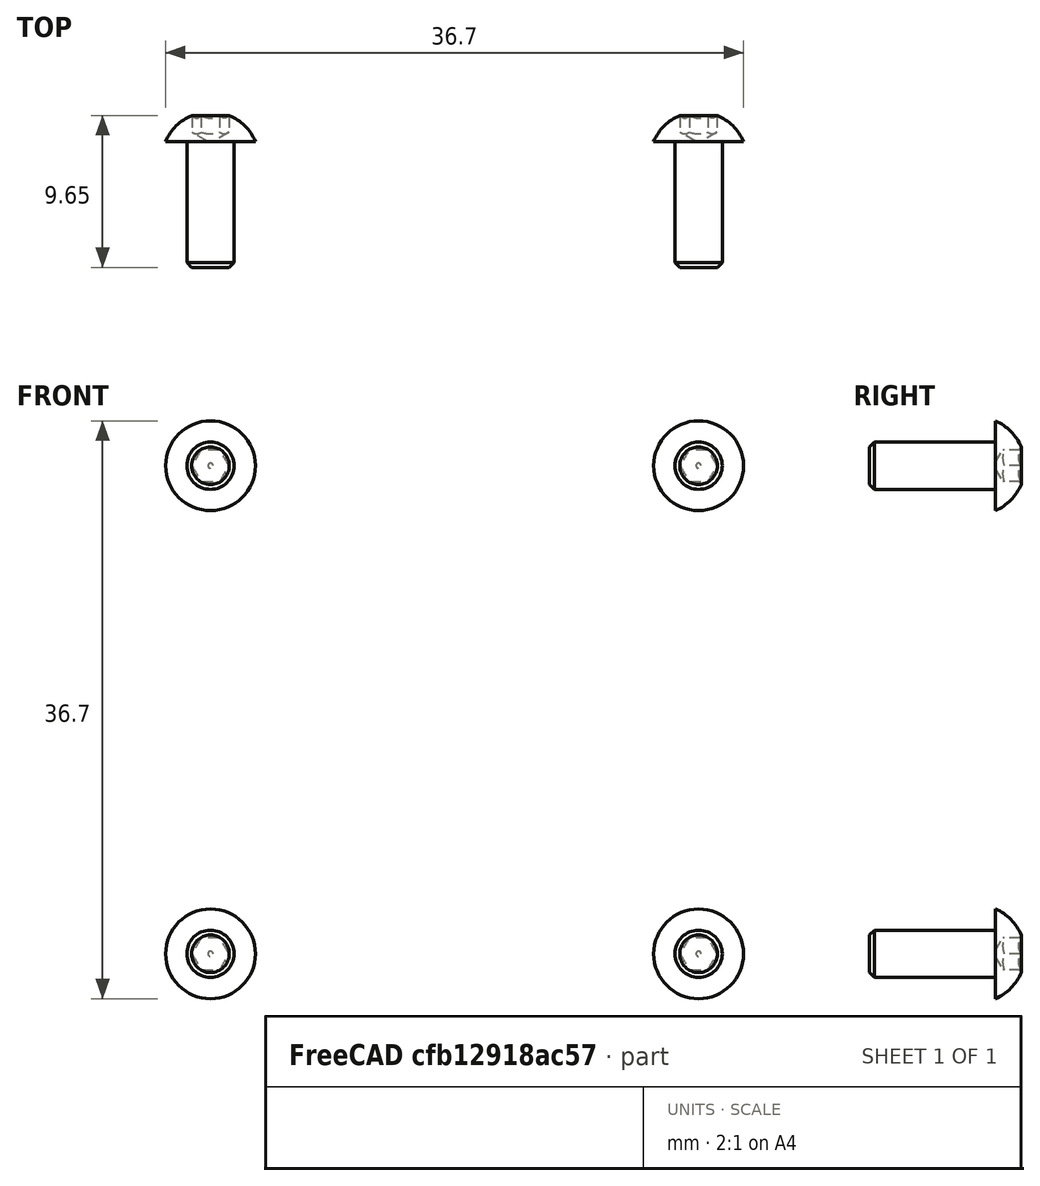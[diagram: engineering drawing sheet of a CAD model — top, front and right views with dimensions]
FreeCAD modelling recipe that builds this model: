
FCSTD DOCUMENT  (FreeCAD 0.20R29410 (Git))
Label: ASM_DriveUnit
License: All rights reserved
LicenseURL: http://en.wikipedia.org/wiki/All_rights_reserved
objects: App::DocumentObjectGroup×4, Part::FeaturePython×4, App::Link×2, PartDesign::CoordinateSystem×1, App::FeaturePython×1, App::Part×1
note: 5 computed .brp shape members not serialized (recipe doc carries the construction recipe); baked Part::Feature solids carry a one-line shape summary decoded from their .brp
EXTERNAL_REF file=ASM_Stepper.FCStd obj=LCS_Origin
EXTERNAL_REF file=ASM_Stepper.FCStd obj=Assembly
EXTERNAL_REF file=ASM_DriveWheel.FCStd obj=LCS_Origin
EXTERNAL_REF file=ASM_Stepper.FCStd obj=Stepper_LCS_mount
EXTERNAL_REF file=ASM_DriveWheel.FCStd obj=Assembly
EXTERNAL_REF file=MotorBracket.FCStd obj=Body001
EXTERNAL_REF file=MotorBracket.FCStd obj=Mirrored001

FEATURE [App::DocumentObjectGroup] Parts
FEATURE [PartDesign::CoordinateSystem] LCS_Origin
  AttacherType = Attacher::AttachEngine3D
  MapMode = 2
  Support = -> [X_Axis]
FEATURE [App::FeaturePython] Variables  # WARN: FeaturePython — macro-defined, semantics opaque (R4)
  Type = App::PropertyContainer
FEATURE [App::DocumentObjectGroup] Constraints
FEATURE [App::DocumentObjectGroup] Configurations
FEATURE [App::Link] ASM_Stepper
  AttachedBy = #LCS_Origin
  AttachedTo = Parent Assembly#LCS_Origin
  LinkedObject = -> <external ASM_Stepper.FCStd>#Assembly
  SolverId = Asm4EE
  expr: Placement = LCS_Origin.Placement * AttachmentOffset * ASM_Stepper#LCS_Origin.Placement ^ -1
FEATURE [App::Link] ASM_DriveWheel
  AttachedBy = #LCS_Origin
  AttachedTo = ASM_Stepper#Stepper_LCS_mount
  AttachmentOffset = pos=(0,0,-14) rot=(0,0,1;0rad)
  LinkPlacement = pos=(0,11,30) rot=(1,0,0;1.5708rad)
  LinkedObject = -> <external ASM_DriveWheel.FCStd>#Assembly
  Placement = pos=(0,11,30) rot=(1,0,0;1.5708rad)
  SolverId = Asm4EE
  expr: Placement = ASM_Stepper.Placement * ASM_Stepper#Stepper_LCS_mount.Placement * AttachmentOffset * ASM_DriveWheel#LCS_Origin.Placement ^ -1
FEATURE [Part::FeaturePython] Screw  label="M3x8-Screw"  # Fasteners workbench fastener (typed FeaturePython)
  Placement = pos=(-15.5,-8.88e-14,45.5) rot=(-1,0,0;1.5708rad)
  baseObject = -> <external MotorBracket.FCStd>#Body001 [Edge90]
  diameter = 1
  invert = true
  length = 1
  lengthCustom = 8
  matchOuter = true
  offset = 0
  thread = false
  type = 40
FEATURE [Part::FeaturePython] Screw001  label="M3x8-Screw007"  # Fasteners workbench fastener (typed FeaturePython)
  Placement = pos=(15.5,-7e-15,45.5) rot=(-1,0,0;1.5708rad)
  baseObject = -> <external MotorBracket.FCStd>#Mirrored001 [Edge87]
  diameter = 1
  invert = true
  length = 1
  lengthCustom = 8
  matchOuter = true
  offset = 0
  thread = false
  type = 40
FEATURE [Part::FeaturePython] Screw002  label="M3x8-Screw008"  # Fasteners workbench fastener (typed FeaturePython)
  Placement = pos=(15.5,-7e-15,14.5) rot=(-1,0,0;1.5708rad)
  baseObject = -> <external MotorBracket.FCStd>#Mirrored001 [Edge88]
  diameter = 1
  invert = true
  length = 1
  lengthCustom = 8
  matchOuter = true
  offset = 0
  thread = false
  type = 40
FEATURE [Part::FeaturePython] Screw003  label="M3x8-Screw009"  # Fasteners workbench fastener (typed FeaturePython)
  Placement = pos=(-15.5,-7e-15,14.5) rot=(-1,0,0;1.5708rad)
  baseObject = -> <external MotorBracket.FCStd>#Mirrored001 [Edge91]
  diameter = 1
  invert = true
  length = 1
  lengthCustom = 8
  matchOuter = true
  offset = 0
  thread = false
  type = 40
FEATURE [App::DocumentObjectGroup] Fasteners
  Group = -> [Screw,Screw001,Screw002,Screw003]
FEATURE [App::Part] Assembly
  AssemblyType = Part::Link
  Group = -> [LCS_Origin,Variables,Constraints,Configurations,ASM_Stepper,ASM_DriveWheel,Fasteners,Screw,Screw001,Screw002,Screw003]
  Origin = -> Origin
  Type = Assembly

RESOLVED EXTERNAL PARTS (link-assembly join: the EXTERNAL_REF files above that resolve inside this repo's crawl, each included once):
---- part ASM_DriveWheel.FCStd = doc fcstd_1d94934c7a89 ----
FCSTD DOCUMENT  (FreeCAD 0.20R29410 (Git))
Label: ASM_DriveWheel
License: All rights reserved
LicenseURL: http://en.wikipedia.org/wiki/All_rights_reserved
objects: App::DocumentObjectGroup×3, App::Link×3, PartDesign::CoordinateSystem×1, App::FeaturePython×1, App::Part×1
note: 1 computed .brp shape members not serialized (recipe doc carries the construction recipe); baked Part::Feature solids carry a one-line shape summary decoded from their .brp
EXTERNAL_REF file=DriveWheelHub.FCStd obj=LCS_Mount
EXTERNAL_REF file=FlangeHub5mm.FCStd obj=LCS_Origin
EXTERNAL_REF file=DriveWheelHub.FCStd obj=Assembly
EXTERNAL_REF file=FlangeHub5mm.FCStd obj=Assembly
EXTERNAL_REF file=DriveWheelHub.FCStd obj=LCS_Origin
EXTERNAL_REF file=DriveWheelTire.FCStd obj=LCS_Origin
EXTERNAL_REF file=DriveWheelTire.FCStd obj=Assembly

FEATURE [App::DocumentObjectGroup] Parts
FEATURE [PartDesign::CoordinateSystem] LCS_Origin
  AttacherType = Attacher::AttachEngine3D
  MapMode = 2
  Support = -> [X_Axis]
FEATURE [App::FeaturePython] Variables  # WARN: FeaturePython — macro-defined, semantics opaque (R4)
  Type = App::PropertyContainer
FEATURE [App::DocumentObjectGroup] Constraints
FEATURE [App::DocumentObjectGroup] Configurations
FEATURE [App::Link] DriveWheelHub
  AttachedBy = #LCS_Mount
  AttachedTo = FlangeHub5mm#LCS_Origin
  AttachmentOffset = pos=(0,0,0) rot=(1,0,0;3.14159rad)
  LinkPlacement = pos=(0,5e-16,2) rot=(0,0,1;0rad)
  LinkedObject = -> <external DriveWheelHub.FCStd>#Assembly
  Placement = pos=(0,5e-16,2) rot=(0,0,1;0rad)
  SolverId = Asm4EE
  expr: Placement = FlangeHub5mm.Placement * FlangeHub5mm#LCS_Origin.Placement * AttachmentOffset * DriveWheelHub#LCS_Mount.Placement ^ -1
FEATURE [App::Link] FlangeHub5mm
  AttachedBy = #LCS_Origin
  AttachedTo = Parent Assembly#LCS_Origin
  AttachmentOffset = pos=(0,0,0) rot=(1,0,0;3.14159rad)
  LinkPlacement = pos=(0,0,0) rot=(1,0,0;3.14159rad)
  LinkedObject = -> <external FlangeHub5mm.FCStd>#Assembly
  Placement = pos=(0,0,0) rot=(1,0,0;3.14159rad)
  SolverId = Asm4EE
  expr: Placement = LCS_Origin.Placement * AttachmentOffset * FlangeHub5mm#LCS_Origin.Placement ^ -1
FEATURE [App::Link] DriveWheelTire
  AttachedBy = #LCS_Origin
  AttachedTo = DriveWheelHub#LCS_Origin
  LinkPlacement = pos=(0,5e-16,2) rot=(0,0,1;0rad)
  LinkedObject = -> <external DriveWheelTire.FCStd>#Assembly
  Placement = pos=(0,5e-16,2) rot=(0,0,1;0rad)
  SolverId = Asm4EE
  expr: Placement = DriveWheelHub.Placement * DriveWheelHub#LCS_Origin.Placement * AttachmentOffset * DriveWheelTire#LCS_Origin.Placement ^ -1
FEATURE [App::Part] Assembly
  AssemblyType = Part::Link
  Group = -> [LCS_Origin,Variables,Constraints,Configurations,DriveWheelHub,FlangeHub5mm,DriveWheelTire]
  Origin = -> Origin
  Type = Assembly
---- part ASM_Stepper.FCStd = doc fcstd_c9ab55faeef8 ----
FCSTD DOCUMENT  (FreeCAD 0.20R29410 (Git))
Label: ASM_Stepper
License: All rights reserved
LicenseURL: http://en.wikipedia.org/wiki/All_rights_reserved
objects: App::DocumentObjectGroup×3, PartDesign::CoordinateSystem×2, App::Link×2, App::FeaturePython×1, App::Part×1
note: 2 computed .brp shape members not serialized (recipe doc carries the construction recipe); baked Part::Feature solids carry a one-line shape summary decoded from their .brp
EXTERNAL_REF file=MotorBracket.FCStd obj=LCS_motor_mount
EXTERNAL_REF file=Stepper17.FCStd obj=LCS_mount
EXTERNAL_REF file=Stepper17.FCStd obj=Body
EXTERNAL_REF file=MotorBracket.FCStd obj=LCS_bottom
EXTERNAL_REF file=MotorBracket.FCStd obj=Assembly

FEATURE [App::DocumentObjectGroup] Parts
FEATURE [PartDesign::CoordinateSystem] LCS_Origin
  AttacherType = Attacher::AttachEngine3D
  MapMode = 2
  Support = -> [X_Axis]
FEATURE [App::FeaturePython] Variables  # WARN: FeaturePython — macro-defined, semantics opaque (R4)
  Type = App::PropertyContainer
FEATURE [App::DocumentObjectGroup] Constraints
FEATURE [App::DocumentObjectGroup] Configurations
FEATURE [App::Link] Stepper
  AssemblyType = Part::Link
  AttachedBy = #LCS_mount
  AttachedTo = MotorBracket#LCS_motor_mount
  LinkPlacement = pos=(0,-3,30) rot=(1,0,0;1.5708rad)
  LinkedObject = -> <external Stepper17.FCStd>#Body
  Placement = pos=(0,-3,30) rot=(1,0,0;1.5708rad)
  SolverId = Asm4EE
  expr: Placement = MotorBracket.Placement * MotorBracket#LCS_motor_mount.Placement * AttachmentOffset * Stepper17#LCS_mount.Placement ^ -1
FEATURE [App::Link] MotorBracket
  AttachedBy = #LCS_bottom
  AttachedTo = Parent Assembly#LCS_Origin
  LinkedObject = -> <external MotorBracket.FCStd>#Assembly
  SolverId = Asm4EE
  expr: Placement = LCS_Origin.Placement * AttachmentOffset * MotorBracket#LCS_bottom.Placement ^ -1
FEATURE [PartDesign::CoordinateSystem] Stepper_LCS_mount
  AttachedBy = Origin
  AttacherType = Attacher::AttachEngine3D
  Placement = pos=(0,-3,30) rot=(1,0,0;1.5708rad)
  SolverId = Asm4EE
  expr: Placement = Stepper.Placement * Stepper17#LCS_mount.Placement
FEATURE [App::Part] Assembly
  AssemblyType = Part::Link
  Group = -> [LCS_Origin,Variables,Constraints,Configurations,Stepper,MotorBracket,Stepper_LCS_mount]
  Origin = -> Origin
  Type = Assembly
---- part MotorBracket.FCStd = doc fcstd_789c5c22f6de ----
FCSTD DOCUMENT  (FreeCAD 0.20R29410 (Git))
Label: MotorBracket
License: All rights reserved
LicenseURL: http://en.wikipedia.org/wiki/All_rights_reserved
objects: Sketcher::SketchObject×5, PartDesign::Pocket×3, App::DocumentObjectGroup×3, PartDesign::Pad×2, PartDesign::Mirrored×2, PartDesign::CoordinateSystem×2, PartDesign::Plane×1, PartDesign::Body×1, App::FeaturePython×1, App::Part×1
note: 21 computed .brp shape members not serialized (recipe doc carries the construction recipe); baked Part::Feature solids carry a one-line shape summary decoded from their .brp

FEATURE [Sketcher::SketchObject] Sketch001
  FullyConstrained = true
  MapMode = 5
  Placement = pos=(0,0,0) rot=(0.57735,0.57735,0.57735;2.0944rad)
  Support = -> [YZ_Plane001]
  expr: Constraints[10] = <<Variables>>.SheetMetalThickness
  sketch-geometry (10):
    g0: LineSegment StartX=-3 StartY=4 StartZ=0 EndX=-3 EndY=51 EndZ=0
    g1: LineSegment StartX=-3 StartY=51 StartZ=0 EndX=0 EndY=51 EndZ=0
    g2: LineSegment StartX=0 StartY=51 StartZ=0 EndX=0 EndY=4 EndZ=0
    g3: LineSegment StartX=-4 StartY=0 StartZ=0 EndX=-51 EndY=0 EndZ=0
    g4: LineSegment StartX=-51 StartY=0 StartZ=0 EndX=-51 EndY=3 EndZ=0
    g5: LineSegment StartX=-51 StartY=3 StartZ=0 EndX=-4 EndY=3 EndZ=0
    g6: ArcOfCircle CenterX=-4 CenterY=4 CenterZ=0 NormalX=0 NormalY=0 NormalZ=1 AngleXU=0 Radius=1 StartAngle=4.71239 EndAngle=6.28319
    g7: GeomPoint X=-3 Y=3 Z=0
    g8: ArcOfCircle CenterX=-4 CenterY=4 CenterZ=0 NormalX=0 NormalY=0 NormalZ=1 AngleXU=0 Radius=4 StartAngle=4.71239 EndAngle=6.28319
    g9: GeomPoint X=0 Y=0 Z=0
  constraints (24):
    c: Coincident(g0,g1)
    c: Coincident(g1,g2)
    c: Horizontal(g1)
    c: Vertical(g0)
    c: Vertical(g2)
    c: Coincident(g3,g4)
    c: Coincident(g4,g5)
    c: Horizontal(g3)
    c: Horizontal(g5)
    c: Vertical(g4)
    c: DistanceX(g1,g1) = 3
    c: DistanceY(g9,g2) = 51
    c: Distance(g9,g3) = 51
    c: Coincident(g9,g-1)
    c: PointOnObject(g7,g0)
    c: PointOnObject(g7,g5)
    c: Tangent(g0,g6) = -1.5708
    c: Tangent(g5,g6) = -1.5708
    c: PointOnObject(g9,g2)
    c: PointOnObject(g9,g3)
    c: Tangent(g2,g8) = 1.5708
    c: Tangent(g3,g8) = 1.5708
    c: Radius(g6) = 1
    c: Coincident(g8,g6)
FEATURE [PartDesign::Pad] Pad001
  Direction = (1,-2e-16,3e-16)
  Length = 51
  Length2 = 25
  Midplane = true
  Placement = pos=(0,0,0) rot=(0.57735,0.57735,0.57735;2.0944rad)
  Profile = -> Sketch001
  ReferenceAxis = -> Sketch001 [N_Axis]
  Type = 0
FEATURE [Sketcher::SketchObject] Sketch002
  AttachmentOffset = pos=(0,30,0) rot=(0,0,1;0rad)
  FullyConstrained = true
  MapMode = 5
  Placement = pos=(0,-6.7e-15,30) rot=(1,0,0;1.5708rad)
  Support = -> [XZ_Plane001]
  sketch-geometry (10):
    g0: Circle CenterX=15.5 CenterY=15.5 CenterZ=0 NormalX=0 NormalY=0 NormalZ=1 AngleXU=0 Radius=1.6
    g1: LineSegment StartX=-15.5 StartY=15.5 StartZ=0 EndX=-15.5 EndY=-15.5 EndZ=0
    g2: LineSegment StartX=-15.5 StartY=-15.5 StartZ=0 EndX=15.5 EndY=-15.5 EndZ=0
    g3: LineSegment StartX=15.5 StartY=-15.5 StartZ=0 EndX=15.5 EndY=15.5 EndZ=0
    g4: LineSegment StartX=15.5 StartY=15.5 StartZ=0 EndX=-15.5 EndY=15.5 EndZ=0
    g5: GeomPoint X=0 Y=0 Z=0
    g6: Circle CenterX=0 CenterY=0 CenterZ=0 NormalX=0 NormalY=0 NormalZ=1 AngleXU=0 Radius=11
    g7: Circle CenterX=-15.5 CenterY=15.5 CenterZ=0 NormalX=0 NormalY=0 NormalZ=1 AngleXU=0 Radius=1.6
    g8: Circle CenterX=-15.5 CenterY=-15.5 CenterZ=0 NormalX=0 NormalY=0 NormalZ=1 AngleXU=0 Radius=1.6
    g9: Circle CenterX=15.5 CenterY=-15.5 CenterZ=0 NormalX=0 NormalY=0 NormalZ=1 AngleXU=0 Radius=1.6
  constraints (22):
    c: Diameter(g0) = 3.2
    c: Coincident(g1,g2)
    c: Coincident(g2,g3)
    c: Coincident(g3,g4)
    c: Coincident(g4,g1)
    c: Horizontal(g2)
    c: Horizontal(g4)
    c: Vertical(g1)
    c: Vertical(g3)
    c: Symmetric(g2,g1,g5)
    c: Equal(g3,g4)
    c: DistanceX(g4,g4) = 31
    c: Coincident(g0,g3)
    c: Coincident(g6,g5)
    c: Diameter(g6) = 22
    c: Coincident(g7,g1)
    c: Coincident(g8,g1)
    c: Coincident(g9,g2)
    c: Equal(g9,g8)
    c: Equal(g8,g7)
    c: Equal(g7,g0)
    c: Coincident(g6,g-1)
FEATURE [PartDesign::Pocket] Pocket001  label="MountHoles"
  BaseFeature = -> Pad001
  Direction = (0,1,2e-16)
  Length = 5
  Length2 = 100
  Placement = pos=(0,0,0) rot=(0.57735,0.57735,0.57735;2.0944rad)
  Profile = -> Sketch002
  Reversed = true
  Type = 1
FEATURE [Sketcher::SketchObject] Sketch003
  FullyConstrained = true
  MapMode = 5
  Support = -> [XY_Plane001]
  sketch-geometry (6):
    g0: LineSegment StartX=-12.865 StartY=0 StartZ=0 EndX=-12.865 EndY=-10.15 EndZ=0
    g1: ArcOfCircle CenterX=-12.865 CenterY=-10.15 CenterZ=0 NormalX=0 NormalY=0 NormalZ=1 AngleXU=0 Radius=2.15 StartAngle=4e-16 EndAngle=3.1416
    g2: ArcOfCircle CenterX=-12.865 CenterY=-39.85 CenterZ=0 NormalX=0 NormalY=0 NormalZ=1 AngleXU=0 Radius=2.15 StartAngle=3.14159 EndAngle=6.28319
    g3: LineSegment StartX=-10.715 StartY=-10.15 StartZ=0 EndX=-10.715 EndY=-39.85 EndZ=0
    g4: LineSegment StartX=-15.015 StartY=-10.15 StartZ=0 EndX=-15.015 EndY=-39.85 EndZ=0
    g5: LineSegment StartX=-12.865 StartY=-39.85 StartZ=0 EndX=0 EndY=-39.85 EndZ=0
  constraints (17):
    c: PointOnObject(g0,g-1)
    c: Vertical(g0)
    c: DistanceY(g0,g0) = 10.15
    c: Coincident(g1,g0)
    c: Equal(g2,g1)
    c: Vertical(g3)
    c: Vertical(g4)
    c: Coincident(g5,g2)
    c: PointOnObject(g5,g-2)
    c: Horizontal(g5)
    c: Tangent(g1,g3) = 1.5708
    c: Coincident(g1,g4)
    c: Tangent(g2,g4) = -1.5708
    c: Tangent(g2,g3) = 1.5708
    c: DistanceX(g5,g5) = 12.865
    c: Distance(g1,g1) = 4.3
    c: Distance(g1,g2) = 29.7
FEATURE [PartDesign::Pocket] Pocket002  label="BottomSlot"
  BaseFeature = -> Pocket001
  Direction = (0,0,-1)
  Length = 5
  Length2 = 100
  Placement = pos=(0,0,0) rot=(0.57735,0.57735,0.57735;2.0944rad)
  Profile = -> Sketch003
  Reversed = true
  Type = 1
FEATURE [Sketcher::SketchObject] Sketch
  AttachmentOffset = pos=(0,0,-25.5) rot=(0,0,1;0rad)
  FullyConstrained = true
  MapMode = 5
  Placement = pos=(-25.5,5.7e-15,-5.7e-15) rot=(0.57735,0.57735,0.57735;2.0944rad)
  Support = -> [YZ_Plane001]
  expr: .AttachmentOffset.Base.z = <<Pad001>>.Length / -2
  sketch-geometry (8):
    g0: LineSegment StartX=-3 StartY=23 StartZ=0 EndX=-23 EndY=3 EndZ=0
    g1: LineSegment StartX=-3 StartY=3 StartZ=0 EndX=-3 EndY=0 EndZ=0
    g2: LineSegment StartX=-3 StartY=0 StartZ=0 EndX=0 EndY=0 EndZ=0
    g3: LineSegment StartX=-3 StartY=3 StartZ=0 EndX=-3 EndY=5 EndZ=0
    g4: LineSegment StartX=-3 StartY=5 StartZ=0 EndX=-3 EndY=23 EndZ=0
    g5: LineSegment StartX=-23 StartY=3 StartZ=0 EndX=-5 EndY=3 EndZ=0
    g6: LineSegment StartX=-5 StartY=3 StartZ=0 EndX=-3 EndY=3 EndZ=0
    g7: LineSegment StartX=-5 StartY=3 StartZ=0 EndX=-3 EndY=5 EndZ=0
  constraints (22):
    c: Coincident(g0,g5)
    c: Coincident(g4,g0)
    c: DistanceY(g3,g4) = 20
    c: Coincident(g3,g6)
    c: DistanceY(g-1,g6) = 3
    c: Coincident(g1,g6)
    c: PointOnObject(g1,g-1)
    c: Coincident(g2,g1)
    c: Coincident(g2,g-1)
    c: Vertical(g1)
    c: Equal(g1,g2)
    c: Coincident(g3,g4)
    c: Vertical(g3)
    c: Vertical(g4)
    c: Coincident(g5,g6)
    c: Horizontal(g5)
    c: Horizontal(g6)
    c: Coincident(g7,g5)
    c: Coincident(g7,g4)
    c: Equal(g3,g6)
    c: DistanceX(g6,g6) = 2
    c: Equal(g4,g5)
FEATURE [PartDesign::Pad] Pad  label="Rib"
  BaseFeature = -> Pocket002
  Direction = (1,-2e-16,3e-16)
  Length = 3
  Length2 = 10
  Placement = pos=(0,0,0) rot=(0.57735,0.57735,0.57735;2.0944rad)
  Profile = -> Sketch
  ReferenceAxis = -> Sketch [N_Axis]
  Type = 0
  expr: Length = <<Variables>>.SheetMetalThickness
FEATURE [PartDesign::Mirrored] Mirrored
  BaseFeature = -> Pad
  MirrorPlane = -> YZ_Plane001
  Originals = -> [Pocket002,Pad]
  Placement = pos=(0,0,0) rot=(0.57735,0.57735,0.57735;2.0944rad)
FEATURE [Sketcher::SketchObject] Sketch004
  FullyConstrained = true
  MapMode = 5
  Placement = pos=(0,0,0) rot=(1,0,0;1.5708rad)
  Support = -> [XZ_Plane001]
  sketch-geometry (6):
    g0: LineSegment StartX=-72.5 StartY=0 StartZ=0 EndX=0 EndY=72.5 EndZ=0
    g1: LineSegment StartX=0 StartY=72.5 StartZ=0 EndX=72.5 EndY=0 EndZ=0
    g2: LineSegment StartX=72.5 StartY=0 StartZ=0 EndX=72.5 EndY=145 EndZ=0
    g3: LineSegment StartX=-72.5 StartY=0 StartZ=0 EndX=-72.5 EndY=145 EndZ=0
    g4: LineSegment StartX=-72.5 StartY=145 StartZ=0 EndX=72.5 EndY=145 EndZ=0
    g5: LineSegment StartX=-21.5 StartY=51 StartZ=0 EndX=21.5 EndY=51 EndZ=0
  constraints (19):
    c: PointOnObject(g0,g-1)
    c: PointOnObject(g0,g-2)
    c: Coincident(g1,g0)
    c: PointOnObject(g1,g-1)
    c: Coincident(g2,g1)
    c: Vertical(g2)
    c: Coincident(g3,g0)
    c: Vertical(g3)
    c: Coincident(g4,g3)
    c: Coincident(g4,g2)
    c: Horizontal(g4)
    c: Equal(g1,g0)
    c: Angle(g1,g-1) = 0.785398
    c: Equal(g2,g4)
    c: PointOnObject(g5,g0)
    c: PointOnObject(g5,g1)
    c: Horizontal(g5)
    c: DistanceY(g-1,g5) = 51
    c: DistanceX(g5,g5) = 43
FEATURE [PartDesign::Pocket] Pocket  label="CornerChamfer"
  BaseFeature = -> Mirrored
  Direction = (0,1,2e-16)
  Length = 5
  Length2 = 5
  Placement = pos=(0,0,0) rot=(0.57735,0.57735,0.57735;2.0944rad)
  Profile = -> Sketch004
  ReferenceAxis = -> Sketch004 [N_Axis]
  Reversed = true
  Type = 1
FEATURE [PartDesign::Plane] DatumPlane  label="ChamferMirrorRef"
  AttachmentOffset = pos=(0,0,0) rot=(1,0,0;0.785398rad)
  Length = 65.8074
  MapMode = 5
  Placement = pos=(0,0,0) rot=(1,0,0;2.35619rad)
  ResizeMode = 0
  Support = -> [XZ_Plane001]
  Width = 122.288
FEATURE [PartDesign::Mirrored] Mirrored001  label="ChamferMirror"
  BaseFeature = -> Pocket
  MirrorPlane = -> DatumPlane
  Originals = -> [Pocket]
  Placement = pos=(0,0,0) rot=(0.57735,0.57735,0.57735;2.0944rad)
FEATURE [PartDesign::Body] Body001
  Group = -> [Sketch001,Pad001,Sketch002,Pocket001,Sketch003,Pocket002,Sketch,Pad,Mirrored,Sketch004,Pocket,DatumPlane,Mirrored001]
  Origin = -> Origin001
  Tip = -> Mirrored001
FEATURE [App::DocumentObjectGroup] Parts
FEATURE [App::FeaturePython] Variables  # WARN: FeaturePython — macro-defined, semantics opaque (R4)
  SheetMetalThickness = 3
  Type = App::PropertyContainer
FEATURE [App::DocumentObjectGroup] Constraints
FEATURE [App::DocumentObjectGroup] Configurations
FEATURE [PartDesign::CoordinateSystem] LCS_bottom
  AttacherType = Attacher::AttachEngine3D
  MapMode = 2
  Support = -> [XY_Plane]
FEATURE [PartDesign::CoordinateSystem] LCS_motor_mount
  AttacherType = Attacher::AttachEngine3D
  AttachmentOffset = pos=(0,0,3) rot=(0,0,1;0rad)
  MapMode = 2
  Placement = pos=(0,-3,30) rot=(1,0,0;1.5708rad)
  Support = -> [Sketch002]
  expr: .AttachmentOffset.Base.z = <<Variables>>.SheetMetalThickness
FEATURE [App::Part] Assembly
  AssemblyType = Part::Link
  Group = -> [Variables,Constraints,Configurations,Body001,LCS_bottom,LCS_motor_mount]
  Origin = -> Origin
  Type = Assembly
